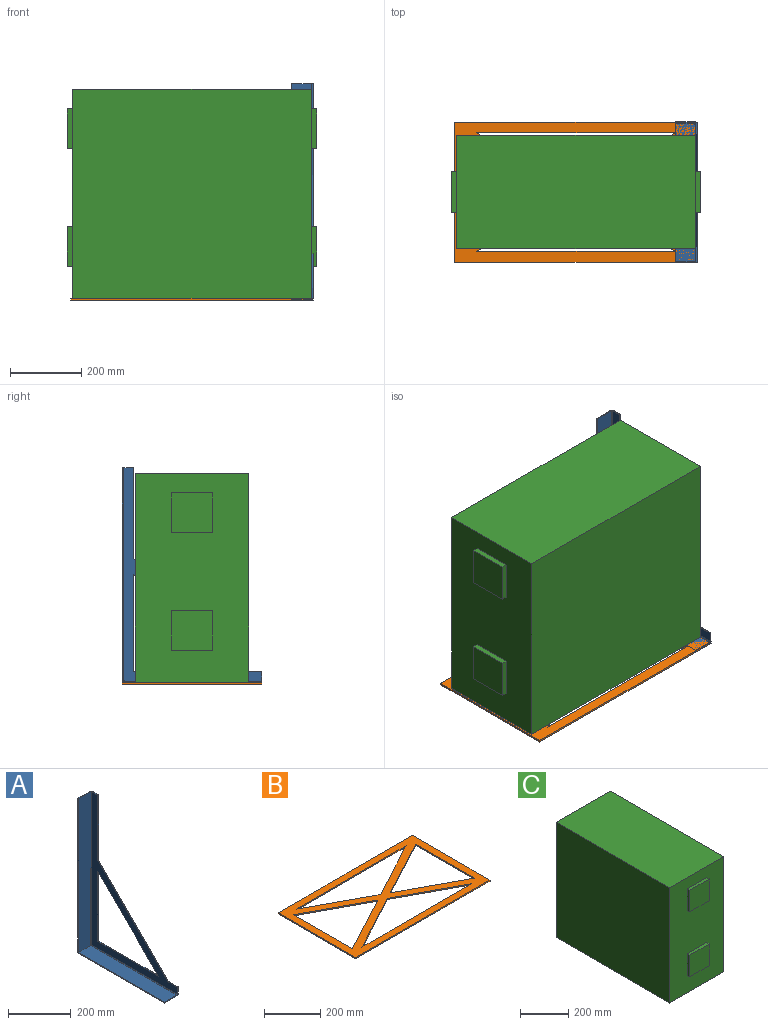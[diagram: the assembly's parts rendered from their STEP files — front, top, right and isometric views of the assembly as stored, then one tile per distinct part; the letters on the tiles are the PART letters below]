
ASSEMBLY  parts=3 mates=3
PART A: 31 faces, bbox 60x391x603 mm
  f0: plane 598x386mm, normal (1,0,0), area 39236.3mm2, adj f1,f2,f3,f4,f5,f6,f7,f8
  f1: plane 28x3mm, normal (0,-1,0), area 84mm2, adj f0,f8,f9,f27
  f2: plane 28x3mm, normal (0,0,1), area 84mm2, adj f0,f3,f9,f17
  f3: plane 254.83x3mm, normal (0,-1,0), area 764.5mm2, adj f0,f2,f4,f9
  f4: plane 315.17x315.17mm, normal (0,-0.71,0.71), area 1337.1mm2, adj f0,f3,f8,f9
  f5: plane 272.74x3mm, normal (0,-1,0), area 818.2mm2, adj f0,f6,f7,f9
  f6: plane 272.74x3mm, normal (0,0,1), area 818.2mm2, adj f0,f5,f7,f9
  f7: plane 272.74x272.74mm, normal (0,0.71,-0.71), area 1157.1mm2, adj f0,f5,f6,f9
  f8: plane 42.83x3mm, normal (0,0,1), area 128.5mm2, adj f0,f1,f4,f9
  f9: plane 598x386mm, normal (-1,0,0), area 39236.3mm2, adj f1,f2,f3,f4,f5,f6,f7,f8
  f10: cylinder r=5.58mm len=3mm, axis (-1,0,0), area 9.9mm2, adj f0,f9,f18,f28
  f11: plane 52.11x3mm, normal (0,0,-1), area 156.3mm2, adj f12,f13,f15,f16
  f12: plane 599.8x55mm, normal (0,1,0), area 32981.1mm2, adj f11,f13,f14,f16,f19
  f13: plane 599.8x3mm, normal (-1,0,0), area 1799.4mm2, adj f11,f12,f14,f15
  f14: plane 55x3mm, normal (0,0,1), area 165mm2, adj f12,f13,f15,f17
  f15: plane 599.8x55mm, normal (0,-1,0), area 32981.1mm2, adj f11,f13,f14,f16,f20
  f16: cylinder r=5.58mm len=4.09mm, axis (0,-1,0), area 15.6mm2, adj f11,f12,f15,f18
  f17: plane 5x5mm, normal (0,0,1), area 16.5mm2, adj f2,f14,f19,f20
  f18: bspline ~5x5mm, area 17.2mm2, adj f10,f16,f19,f20
  f19: cylinder r=5mm len=595.71mm, axis (0,0,1), area 4675.2mm2, adj f0,f12,f17,f18
  f20: cylinder r=2mm len=595.71mm, axis (0,0,1), area 1870.1mm2, adj f9,f15,f17,f18
  f21: plane 52.11x3mm, normal (0,1,0), area 156.3mm2, adj f22,f23,f25,f26
  f22: plane 387.8x55mm, normal (0,0,-1), area 21321.1mm2, adj f21,f23,f24,f26,f29
  f23: plane 387.8x3mm, normal (-1,0,0), area 1163.4mm2, adj f21,f22,f24,f25
  f24: plane 55x3mm, normal (0,-1,0), area 165mm2, adj f22,f23,f25,f27
  f25: plane 387.8x55mm, normal (0,0,1), area 21321.1mm2, adj f21,f23,f24,f26,f30
  f26: cylinder r=5.58mm len=4.09mm, axis (0,0,1), area 15.6mm2, adj f21,f22,f25,f28
  f27: plane 5x5mm, normal (0,-1,0), area 16.5mm2, adj f1,f24,f29,f30
  f28: bspline ~5x5mm, area 17.2mm2, adj f10,f26,f29,f30
  f29: cylinder r=5mm len=383.71mm, axis (0,1,0), area 3010.1mm2, adj f0,f22,f27,f28
  f30: cylinder r=2mm len=383.71mm, axis (0,1,0), area 1204.1mm2, adj f9,f25,f27,f28
PART B: 18 faces, bbox 678x392x5 mm
  f0: plane 297.95x5mm, normal (1,0,0), area 1489.7mm2, adj f1,f15,f16,f17
  f1: plane 277.3x148.97mm, normal (-0.47,0.88,0), area 1573.9mm2, adj f0,f15,f16,f17
  f2: plane 554.61x5mm, normal (0,-1,0), area 2773mm2, adj f3,f14,f16,f17
  f3: plane 277.3x148.97mm, normal (0.47,0.88,0), area 1573.9mm2, adj f2,f14,f16,f17
  f4: plane 277.3x148.97mm, normal (0.47,-0.88,0), area 1573.9mm2, adj f5,f13,f16,f17
  f5: plane 554.61x5mm, normal (0,1,0), area 2773mm2, adj f4,f13,f16,f17
  f6: plane 277.3x148.97mm, normal (0.47,0.88,0), area 1573.9mm2, adj f7,f12,f16,f17
  f7: plane 297.95x5mm, normal (-1,0,0), area 1489.7mm2, adj f6,f12,f16,f17
  f8: plane 678x5mm, normal (0,-1,0), area 3390mm2, adj f9,f11,f16,f17
  f9: plane 392x5mm, normal (-1,0,0), area 1960mm2, adj f8,f10,f16,f17
  f10: plane 678x5mm, normal (0,1,0), area 3390mm2, adj f9,f11,f16,f17
  f11: plane 392x5mm, normal (1,0,0), area 1960mm2, adj f8,f10,f16,f17
  f12: plane 277.3x148.97mm, normal (0.47,-0.88,0), area 1573.9mm2, adj f6,f7,f16,f17
  f13: plane 277.3x148.97mm, normal (-0.47,-0.88,0), area 1573.9mm2, adj f4,f5,f16,f17
  f14: plane 277.3x148.97mm, normal (-0.47,0.88,0), area 1573.9mm2, adj f2,f3,f16,f17
  f15: plane 277.3x148.97mm, normal (-0.47,-0.88,0), area 1573.9mm2, adj f0,f1,f16,f17
  f16: plane 678x392mm, normal (0,0,-1), area 100533.2mm2, adj f0,f1,f2,f3,f4,f5,f6,f7
  f17: plane 678x392mm, normal (0,0,1), area 100533.2mm2, adj f0,f1,f2,f3,f4,f5,f6,f7
PART C: 26 faces, bbox 317x698x585 mm
  f0: plane 585x317mm, normal (0,-1,0), area 160145mm2, adj f1,f2,f3,f4,f6,f7,f8,f9
  f1: plane 668x585mm, normal (-1,0,0), area 390780mm2, adj f0,f2,f4,f5
  f2: plane 668x317mm, normal (0,0,-1), area 211756mm2, adj f0,f1,f3,f5
  f3: plane 668x585mm, normal (1,0,0), area 390780mm2, adj f0,f2,f4,f5
  f4: plane 668x317mm, normal (0,0,1), area 211756mm2, adj f0,f1,f3,f5
  f5: plane 585x317mm, normal (0,1,0), area 160145mm2, adj f1,f2,f3,f4,f16,f17,f18,f19
  f6: plane 115x15mm, normal (0,0,-1), area 1725mm2, adj f0,f7,f9,f10
  f7: plane 110x15mm, normal (1,0,0), area 1650mm2, adj f0,f6,f8,f10
  f8: plane 115x15mm, normal (0,0,1), area 1725mm2, adj f0,f7,f9,f10
  f9: plane 110x15mm, normal (-1,0,0), area 1650mm2, adj f0,f6,f8,f10
  f10: plane 115x110mm, normal (0,-1,0), area 12650mm2, adj f6,f7,f8,f9
  f11: plane 115x15mm, normal (0,0,-1), area 1725mm2, adj f0,f12,f14,f15
  f12: plane 110x15mm, normal (1,0,0), area 1650mm2, adj f0,f11,f13,f15
  f13: plane 115x15mm, normal (0,0,1), area 1725mm2, adj f0,f12,f14,f15
  f14: plane 110x15mm, normal (-1,0,0), area 1650mm2, adj f0,f11,f13,f15
  f15: plane 115x110mm, normal (0,-1,0), area 12650mm2, adj f11,f12,f13,f14
  f16: plane 115x15mm, normal (0,0,-1), area 1725mm2, adj f5,f17,f19,f20
  f17: plane 110x15mm, normal (-1,0,0), area 1650mm2, adj f5,f16,f18,f20
  f18: plane 115x15mm, normal (0,0,1), area 1725mm2, adj f5,f17,f19,f20
  f19: plane 110x15mm, normal (1,0,0), area 1650mm2, adj f5,f16,f18,f20
  f20: plane 115x110mm, normal (0,1,0), area 12650mm2, adj f16,f17,f18,f19
  f21: plane 115x15mm, normal (0,0,-1), area 1725mm2, adj f5,f22,f24,f25
  f22: plane 110x15mm, normal (-1,0,0), area 1650mm2, adj f5,f21,f23,f25
  f23: plane 115x15mm, normal (0,0,1), area 1725mm2, adj f5,f22,f24,f25
  f24: plane 110x15mm, normal (1,0,0), area 1650mm2, adj f5,f21,f23,f25
  f25: plane 115x110mm, normal (0,1,0), area 12650mm2, adj f21,f22,f23,f24
PLACE A t=(336,-195,5)mm
PLACE B t=(-58.31,-49.17,0)mm
PLACE C rot(axis=(0,0,1),90deg) t=(0,-158.5,5)mm
MATE fastened C.f2 <-> B.f17  axis (0,0,-1) through (0,0,5)mm
MATE planar A.f0 <-> B.f11  axis (1,0,0) through (339,76.44,193.87)mm
MATE parallel A.f0 <-> B.f11  axis (1,0,0) through (339,76.44,193.87)mm
